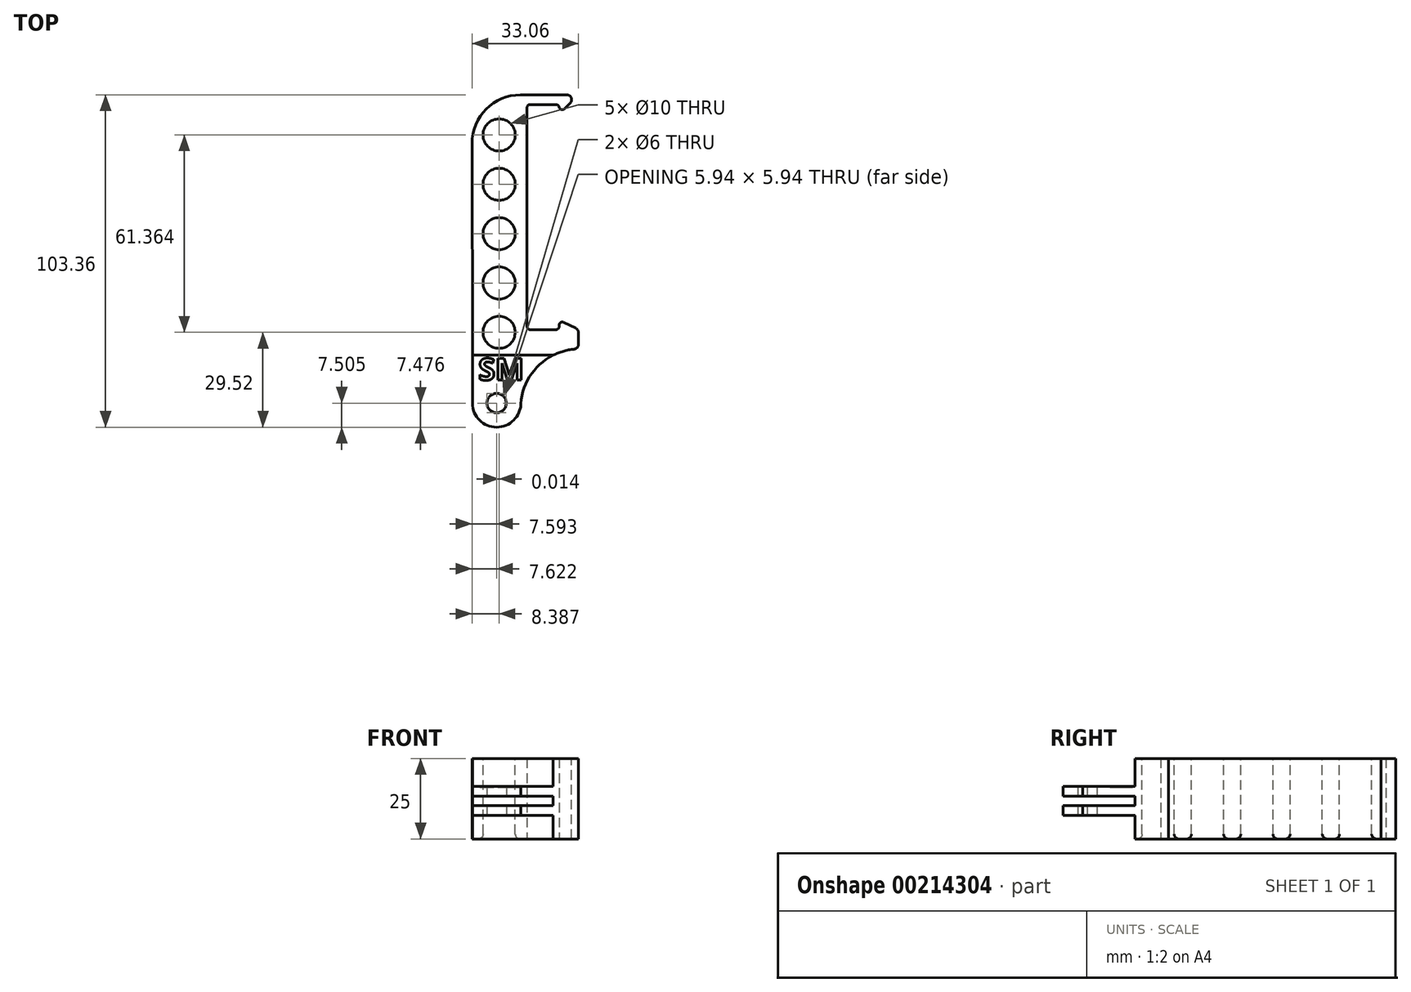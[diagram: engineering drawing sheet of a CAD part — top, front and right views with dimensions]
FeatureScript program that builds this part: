
annotation { "Feature Type Name" : "Feature", "Feature Type Description" : "" }
export const myFeature = defineFeature(function(context is Context, id is Id, definition is map)
    precondition{}
    {
        {
            var Q0;
            Q0=qCreatedBy(makeId("Top.planeOp"),FACE);
            var sketch = newSketch(context, id + "F0", { "sketchPlane" : qUnion([Q0])});
            skLineSegment(sketch, "E0.right", {"start": v(-6.96, 70) * mm, "end": v(-6.96, 0) * mm});
            skLineSegment(sketch, "E1.bottom", {"start": v(-6.96, 0) * mm, "end": v(3.04, 0) * mm});
            skLineSegment(sketch, "E1.right", {"start": v(9.04, 0) * mm, "end": v(9.04, -6) * mm});
            skLineSegment(sketch, "E2.bottom", {"start": v(-6.96, 70) * mm, "end": v(3.04, 70) * mm});
            skLineSegment(sketch, "E2.top", {"start": v(-9, 73) * mm, "end": v(9.04, 73) * mm});
            skLineSegment(sketch, "E3.left", {"start": v(3.04, 70) * mm, "end": v(3.04, 67) * mm});
            skLineSegment(sketch, "E4.left", {"start": v(3.04, 0) * mm, "end": v(3.04, 3) * mm});
            skLineSegment(sketch, "E5.left", {"start": v(-23.9, -7.86) * mm, "end": v(-23.9, -22.86) * mm});
            skLineSegment(sketch, "E5.right", {"start": v(-8.9, -22.86) * mm, "end": v(-8.9, -24.26) * mm});
            skArc(sketch, "E6", {"start": v(-23.9, -22.86) * mm, "mid": v(-16.4, -30.36) * mm, "end": v(-8.9, -22.86) * mm});
            skCircle(sketch, "E7", {"center": v(-16.4, -22.86) * mm, "radius": 3 * mm});
            skPoint(sketch, "E1.top.start.orphan", {"position": v(3.04, -3.63) * mm});
            skLineSegment(sketch, "E8", {"start": v(9.04, 0) * mm, "end": v(3.04, 3) * mm});
            skArc(sketch, "E9", {"start": v(9.04, -6) * mm, "mid": v(-3.66, -11.47) * mm, "end": v(-8.9, -24.26) * mm});
            skPoint(sketch, "E4.right.end.orphan", {"position": v(9.04, -0.42) * mm});
            skLineSegment(sketch, "E10", {"start": v(3.04, 67) * mm, "end": v(9.04, 73) * mm});
            skLineSegment(sketch, "E11.left", {"start": v(-23.9, -7.86) * mm, "end": v(-24.02, 57.9) * mm});
            skArc(sketch, "E12", {"start": v(-9, 73) * mm, "mid": v(-19.63, 68.55) * mm, "end": v(-24.02, 57.9) * mm});
            skSolve(sketch);
        }
        {
            var Q0;
            {var subQ0=sQuery(id+"F0.wireOp",EDGE,"E11.top");Q0=makeQuery(id+"F0.imprint","IMPRINT",FACE,{"disambiguationData":[TD([[makeQuery(id+"F0.imprint","IMPRINT",EDGE,{"derivedFrom":subQ0}),-1.0]])]});}
            var Q1;
            Q1=makeQuery(id+"F0.imprint","IMPRINT",FACE,{"disambiguationData":[TD([[makeQuery(id+"F0.imprint","IMPRINT",EDGE,{"derivedFrom":sQuery(id+"F0.wireOp",EDGE,"E0.right")}),-1.0]])]});
            var Q2;
            {var subQ0=sQuery(id+"F0.wireOp",EDGE,"E11.bottom");Q2=makeQuery(id+"F0.imprint","IMPRINT",FACE,{"disambiguationData":[TD([[makeQuery(id+"F0.imprint","IMPRINT",EDGE,{"derivedFrom":subQ0}),1.0]])]});}
            extrude(context, id + "F1", {"entities" : qUnion([Q0, Q1, Q2]), "depth" : 25 * mm});
        }
        {
            var Q0;
            Q0=makeQuery(id+"F1.opExtrude","SWEPT_FACE",FACE,{"disambiguationData":[OSD([sQuery(id+"F0.wireOp",EDGE,"E5.left")])]});
            var sketch = newSketch(context, id + "F2", { "sketchPlane" : qUnion([Q0])});
            skLineSegment(sketch, "E13.bottom", {"start": v(39.47, 13.32) * mm, "end": v(7.86, 13.32) * mm});
            skLineSegment(sketch, "E13.top", {"start": v(39.47, 10.32) * mm, "end": v(7.86, 10.32) * mm});
            skLineSegment(sketch, "E13.left", {"start": v(7.86, 13.32) * mm, "end": v(7.86, 10.32) * mm});
            skLineSegment(sketch, "E13.right", {"start": v(39.47, 13.32) * mm, "end": v(39.47, 10.32) * mm});
            skLineSegment(sketch, "E14.bottom", {"start": v(7.86, 13.32) * mm, "end": v(39.63, 13.32) * mm});
            skLineSegment(sketch, "E14.top", {"start": v(7.86, 16.32) * mm, "end": v(39.63, 16.32) * mm});
            skLineSegment(sketch, "E14.left", {"start": v(7.86, 13.32) * mm, "end": v(7.86, 16.32) * mm});
            skLineSegment(sketch, "E14.right", {"start": v(39.63, 13.32) * mm, "end": v(39.63, 16.32) * mm});
            skLineSegment(sketch, "E15.bottom", {"start": v(7.86, 10.32) * mm, "end": v(39.63, 10.32) * mm});
            skLineSegment(sketch, "E15.top", {"start": v(7.86, 7.32) * mm, "end": v(39.63, 7.32) * mm});
            skLineSegment(sketch, "E15.left", {"start": v(7.86, 10.32) * mm, "end": v(7.86, 7.32) * mm});
            skLineSegment(sketch, "E15.right", {"start": v(39.63, 10.32) * mm, "end": v(39.63, 7.32) * mm});
            skLineSegment(sketch, "E16.top", {"start": v(7.86, 38.98) * mm, "end": v(39.63, 38.98) * mm});
            skLineSegment(sketch, "E16.left", {"start": v(7.86, 16.32) * mm, "end": v(7.86, 38.98) * mm});
            skLineSegment(sketch, "E16.right", {"start": v(39.63, 16.32) * mm, "end": v(39.63, 38.98) * mm});
            skLineSegment(sketch, "E17.top", {"start": v(7.86, -18.68) * mm, "end": v(39.63, -18.68) * mm});
            skLineSegment(sketch, "E17.left", {"start": v(7.86, 7.32) * mm, "end": v(7.86, -18.68) * mm});
            skLineSegment(sketch, "E17.right", {"start": v(39.63, 7.32) * mm, "end": v(39.63, -18.68) * mm});
            skSolve(sketch);
        }
        {
            var Q0;
            {var subQ1=sQuery(id+"F0.wireOp",EDGE,"E5.left");var subQ6=makeQuery(id+"F1.opExtrude","CAP_EDGE",EDGE,{"disambiguationData":[OSD([subQ1])],"isStart":true});Q0=makeQuery(id+"F2.imprint","IMPRINT",FACE,{"disambiguationData":[TD([[makeQuery(id+"F2.imprint","IMPRINT",EDGE,{"derivedFrom":subQ6}),1.0]])]});}
            var Q1;
            {var subQ1=sQuery(id+"F0.wireOp",EDGE,"E5.left");var subQ6=makeQuery(id+"F1.opExtrude","CAP_EDGE",EDGE,{"disambiguationData":[OSD([subQ1])],"isStart":false});Q1=makeQuery(id+"F2.imprint","IMPRINT",FACE,{"disambiguationData":[TD([[makeQuery(id+"F2.imprint","IMPRINT",EDGE,{"derivedFrom":subQ6}),-1.0]])]});}
            var Q2;
            {var subQ1=sQuery(id+"F2.wireOp",EDGE,"E17.top");Q2=makeQuery(id+"F2.imprint","IMPRINT",FACE,{"disambiguationData":[TD([[makeQuery(id+"F2.imprint","IMPRINT",EDGE,{"derivedFrom":subQ1}),1.0]])]});}
            var Q3;
            {var subQ4=sQuery(id+"F2.wireOp",EDGE,"E16.top");Q3=makeQuery(id+"F2.imprint","IMPRINT",FACE,{"disambiguationData":[TD([[makeQuery(id+"F2.imprint","IMPRINT",EDGE,{"derivedFrom":subQ4}),-1.0]])]});}
            var Q4;
            {var subQ0=sQuery(id+"F2.wireOp",EDGE,"E13.right");Q4=makeQuery(id+"F2.imprint","IMPRINT",FACE,{"disambiguationData":[TD([[makeQuery(id+"F2.imprint","IMPRINT",EDGE,{"derivedFrom":subQ0}),-1.0]])]});}
            var Q5;
            {var subQ0=sQuery(id+"F2.wireOp",EDGE,"E13.left");Q5=makeQuery(id+"F2.imprint","IMPRINT",FACE,{"disambiguationData":[TD([[makeQuery(id+"F2.imprint","IMPRINT",EDGE,{"derivedFrom":subQ0}),1.0]])]});}
            extrude(context, id + "F3", {"entities" : qUnion([Q0, Q1, Q2, Q3, Q4, Q5]), "operationType" : NewBodyOperationType.REMOVE, "oppositeDirection" : true, "depth" : 25 * mm});
        }
        {
            var Q0;
            Q0=makeQuery(id+"F1.opExtrude","SWEPT_EDGE",EDGE,{"disambiguationData":[OSD([sQuery(id+"F0.wireOp",EDGE,"E1.right"),sQuery(id+"F0.wireOp",EDGE,"E8")])]});
            var Q1;
            Q1=makeQuery(id+"F1.opExtrude","SWEPT_EDGE",EDGE,{"disambiguationData":[OSD([sQuery(id+"F0.wireOp",EDGE,"E1.right"),sQuery(id+"F0.wireOp",EDGE,"E9")])]});
            var Q2;
            Q2=makeQuery(id+"F1.opExtrude","SWEPT_EDGE",EDGE,{"disambiguationData":[OSD([sQuery(id+"F0.wireOp",EDGE,"E2.top"),sQuery(id+"F0.wireOp",EDGE,"E10")])]});
            fillet(context, id + "F4", {"entities" : qUnion([Q0, Q1, Q2]), "radius" : 1.5 * mm, "tangentPropagation" : true, "allowEdgeOverflow" : false});
        }
        {
            var Q0;
            Q0=makeQuery(id+"F1.opExtrude","SWEPT_EDGE",EDGE,{"disambiguationData":[OSD([sQuery(id+"F0.wireOp",EDGE,"E0.right"),sQuery(id+"F0.wireOp",EDGE,"E2.bottom")])]});
            var Q1;
            Q1=makeQuery(id+"F1.opExtrude","SWEPT_EDGE",EDGE,{"disambiguationData":[OSD([sQuery(id+"F0.wireOp",EDGE,"E0.right"),sQuery(id+"F0.wireOp",EDGE,"E1.bottom")])]});
            var Q2;
            Q2=makeQuery(id+"F1.opExtrude","SWEPT_EDGE",EDGE,{"disambiguationData":[OSD([sQuery(id+"F0.wireOp",EDGE,"E2.bottom"),sQuery(id+"F0.wireOp",EDGE,"E3.left")])]});
            var Q3;
            Q3=makeQuery(id+"F1.opExtrude","SWEPT_EDGE",EDGE,{"disambiguationData":[OSD([sQuery(id+"F0.wireOp",EDGE,"E1.bottom"),sQuery(id+"F0.wireOp",EDGE,"E4.left")])]});
            fillet(context, id + "F5", {"entities" : qUnion([Q0, Q1, Q2, Q3]), "radius" : 1 * mm, "tangentPropagation" : true, "allowEdgeOverflow" : false});
        }
        {
            var Q0;
            Q0=makeQuery(id+"F1.opExtrude","CAP_FACE",FACE,{"disambiguationData":[OSD([sQuery(id+"F0.wireOp",EDGE,"E0.right"),sQuery(id+"F0.wireOp",EDGE,"E1.bottom"),sQuery(id+"F0.wireOp",EDGE,"E1.right"),sQuery(id+"F0.wireOp",EDGE,"E2.bottom"),sQuery(id+"F0.wireOp",EDGE,"E2.top"),sQuery(id+"F0.wireOp",EDGE,"E2.right"),sQuery(id+"F0.wireOp",EDGE,"E3.top"),sQuery(id+"F0.wireOp",EDGE,"E3.left"),sQuery(id+"F0.wireOp",EDGE,"E4.top"),sQuery(id+"F0.wireOp",EDGE,"E4.left"),sQuery(id+"F0.wireOp",EDGE,"E5.left"),sQuery(id+"F0.wireOp",EDGE,"E5.right"),sQuery(id+"F0.wireOp",EDGE,"E6"),sQuery(id+"F0.wireOp",EDGE,"E7"),sQuery(id+"F0.wireOp",EDGE,"vfLY6uG4-y0tV-8spB-1rVG-UtVCXCo2wCze"),sQuery(id+"F0.wireOp",EDGE,"IZeYfrJS-7V4p-GKvK-Bs6F-KUIEGbjNp2gk"),sQuery(id+"F0.wireOp",EDGE,"UbSuR1B7-Qmw8-mbvo-CxSJ-8DXWhNlOWwhV"),sQuery(id+"F0.wireOp",EDGE,"E8"),sQuery(id+"F0.wireOp",EDGE,"E9"),sQuery(id+"F0.wireOp",EDGE,"E10"),sQuery(id+"F0.wireOp",EDGE,"E11.top"),sQuery(id+"F0.wireOp",EDGE,"E11.left")])],"isStart":false});
            var sketch = newSketch(context, id + "F6", { "sketchPlane" : qUnion([Q0])});
            skLineSegment(sketch, "E18", {"start": v(21.8, 35) * mm, "end": v(-35.74, 35) * mm, "construction": true});
            skLineSegment(sketch, "E19", {"start": v(-15.63, 69.17) * mm, "end": v(-15.43, -43.11) * mm, "construction": true});
            skCircle(sketch, "E20", {"center": v(-15.62, 60.52) * mm, "radius": 5 * mm});
            skCircle(sketch, "E21.0.1.0", {"center": v(-15.62, 45.18) * mm, "radius": 5 * mm});
            skCircle(sketch, "E21.0.2.0", {"center": v(-15.63, 29.84) * mm, "radius": 5 * mm});
            skCircle(sketch, "E21.0.3.0", {"center": v(-15.63, 14.5) * mm, "radius": 5 * mm});
            skCircle(sketch, "E21.0.4.0", {"center": v(-15.63, -0.84) * mm, "radius": 5 * mm});
            skLineSegment(sketch, "E21.direction1", {"start": v(-15.62, 60.52) * mm, "end": v(10.9, 60.52) * mm, "construction": true});
            skLineSegment(sketch, "E21.direction2", {"start": v(-15.62, 60.52) * mm, "end": v(-15.62, 45.18) * mm, "construction": true});
            skSolve(sketch);
        }
        {
            var Q0;
            Q0=makeQuery(id+"F6.imprint","IMPRINT",FACE,{"disambiguationData":[TD([[makeQuery(id+"F6.imprint","IMPRINT",EDGE,{"derivedFrom":sQuery(id+"F6.wireOp",EDGE,"E20")}),1.0]])]});
            var Q1;
            Q1=makeQuery(id+"F6.imprint","IMPRINT",FACE,{"disambiguationData":[TD([[makeQuery(id+"F6.imprint","IMPRINT",EDGE,{"derivedFrom":sQuery(id+"F6.wireOp",EDGE,"E21.0.1.0")}),1.0]])]});
            var Q2;
            Q2=makeQuery(id+"F6.imprint","IMPRINT",FACE,{"disambiguationData":[TD([[makeQuery(id+"F6.imprint","IMPRINT",EDGE,{"derivedFrom":sQuery(id+"F6.wireOp",EDGE,"E21.0.3.0")}),1.0]])]});
            var Q3;
            Q3=makeQuery(id+"F6.imprint","IMPRINT",FACE,{"disambiguationData":[TD([[makeQuery(id+"F6.imprint","IMPRINT",EDGE,{"derivedFrom":sQuery(id+"F6.wireOp",EDGE,"E21.0.4.0")}),1.0]])]});
            var Q4;
            Q4=makeQuery(id+"F6.imprint","IMPRINT",FACE,{"disambiguationData":[TD([[makeQuery(id+"F6.imprint","IMPRINT",EDGE,{"derivedFrom":sQuery(id+"F6.wireOp",EDGE,"E21.0.2.0")}),1.0]])]});
            extrude(context, id + "F7", {"entities" : qUnion([Q0, Q1, Q2, Q3, Q4]), "operationType" : NewBodyOperationType.REMOVE, "oppositeDirection" : true, "depth" : 25 * mm});
        }
        {
            var Q0;
            Q0=makeQuery(id+"F1.opExtrude","SWEPT_EDGE",EDGE,{"disambiguationData":[OSD([sQuery(id+"F0.wireOp",EDGE,"E3.left"),sQuery(id+"F0.wireOp",EDGE,"E10")])]});
            var Q1;
            Q1=makeQuery(id+"F1.opExtrude","SWEPT_EDGE",EDGE,{"disambiguationData":[OSD([sQuery(id+"F0.wireOp",EDGE,"E4.left"),sQuery(id+"F0.wireOp",EDGE,"E8")])]});
            fillet(context, id + "F8", {"entities" : qUnion([Q0, Q1]), "radius" : 1 * mm, "tangentPropagation" : true, "allowEdgeOverflow" : false});
        }
        {
            var Q0;
            Q0=makeQuery(id+"F7.boolean.opBoolean","COPY",EDGE,{"derivedFrom":makeQuery(id+"F7.opExtrude","CAP_EDGE",EDGE,{"disambiguationData":[OSD([sQuery(id+"F6.wireOp",EDGE,"E20")])],"isStart":true})});
            var Q1;
            Q1=makeQuery(id+"F7.boolean.opBoolean","COPY",EDGE,{"derivedFrom":makeQuery(id+"F7.opExtrude","CAP_EDGE",EDGE,{"disambiguationData":[OSD([sQuery(id+"F6.wireOp",EDGE,"E21.0.1.0")])],"isStart":true})});
            var Q2;
            Q2=makeQuery(id+"F7.boolean.opBoolean","COPY",EDGE,{"derivedFrom":makeQuery(id+"F7.opExtrude","CAP_EDGE",EDGE,{"disambiguationData":[OSD([sQuery(id+"F6.wireOp",EDGE,"E21.0.2.0")])],"isStart":true})});
            var Q3;
            Q3=makeQuery(id+"F7.boolean.opBoolean","COPY",EDGE,{"derivedFrom":makeQuery(id+"F7.opExtrude","CAP_EDGE",EDGE,{"disambiguationData":[OSD([sQuery(id+"F6.wireOp",EDGE,"E21.0.3.0")])],"isStart":true})});
            var Q4;
            Q4=makeQuery(id+"F7.boolean.opBoolean","COPY",EDGE,{"derivedFrom":makeQuery(id+"F7.opExtrude","CAP_EDGE",EDGE,{"disambiguationData":[OSD([sQuery(id+"F6.wireOp",EDGE,"E21.0.4.0")])],"isStart":true})});
            var Q5;
            Q5=makeQuery(id+"F7.boolean.opBoolean","INTERSECT",EDGE,{"derivedFrom":[makeQuery(id+"F1.opExtrude","CAP_FACE",FACE,{"disambiguationData":[OSD([sQuery(id+"F0.wireOp",EDGE,"E0.right"),sQuery(id+"F0.wireOp",EDGE,"E1.bottom"),sQuery(id+"F0.wireOp",EDGE,"E1.right"),sQuery(id+"F0.wireOp",EDGE,"E2.bottom"),sQuery(id+"F0.wireOp",EDGE,"E2.top"),sQuery(id+"F0.wireOp",EDGE,"E3.left"),sQuery(id+"F0.wireOp",EDGE,"E4.left"),sQuery(id+"F0.wireOp",EDGE,"E5.left"),sQuery(id+"F0.wireOp",EDGE,"E6"),sQuery(id+"F0.wireOp",EDGE,"E7"),sQuery(id+"F0.wireOp",EDGE,"E8"),sQuery(id+"F0.wireOp",EDGE,"E9"),sQuery(id+"F0.wireOp",EDGE,"E10"),sQuery(id+"F0.wireOp",EDGE,"E11.left"),sQuery(id+"F0.wireOp",EDGE,"E12")])],"isStart":true}),makeQuery(id+"F7.opExtrude","SWEPT_FACE",FACE,{"disambiguationData":[OSD([sQuery(id+"F6.wireOp",EDGE,"E20")])]})]});
            var Q6;
            Q6=makeQuery(id+"F7.boolean.opBoolean","INTERSECT",EDGE,{"derivedFrom":[makeQuery(id+"F1.opExtrude","CAP_FACE",FACE,{"disambiguationData":[OSD([sQuery(id+"F0.wireOp",EDGE,"E0.right"),sQuery(id+"F0.wireOp",EDGE,"E1.bottom"),sQuery(id+"F0.wireOp",EDGE,"E1.right"),sQuery(id+"F0.wireOp",EDGE,"E2.bottom"),sQuery(id+"F0.wireOp",EDGE,"E2.top"),sQuery(id+"F0.wireOp",EDGE,"E3.left"),sQuery(id+"F0.wireOp",EDGE,"E4.left"),sQuery(id+"F0.wireOp",EDGE,"E5.left"),sQuery(id+"F0.wireOp",EDGE,"E6"),sQuery(id+"F0.wireOp",EDGE,"E7"),sQuery(id+"F0.wireOp",EDGE,"E8"),sQuery(id+"F0.wireOp",EDGE,"E9"),sQuery(id+"F0.wireOp",EDGE,"E10"),sQuery(id+"F0.wireOp",EDGE,"E11.left"),sQuery(id+"F0.wireOp",EDGE,"E12")])],"isStart":true}),makeQuery(id+"F7.opExtrude","SWEPT_FACE",FACE,{"disambiguationData":[OSD([sQuery(id+"F6.wireOp",EDGE,"E21.0.1.0")])]})]});
            var Q7;
            Q7=makeQuery(id+"F7.boolean.opBoolean","INTERSECT",EDGE,{"derivedFrom":[makeQuery(id+"F1.opExtrude","CAP_FACE",FACE,{"disambiguationData":[OSD([sQuery(id+"F0.wireOp",EDGE,"E0.right"),sQuery(id+"F0.wireOp",EDGE,"E1.bottom"),sQuery(id+"F0.wireOp",EDGE,"E1.right"),sQuery(id+"F0.wireOp",EDGE,"E2.bottom"),sQuery(id+"F0.wireOp",EDGE,"E2.top"),sQuery(id+"F0.wireOp",EDGE,"E3.left"),sQuery(id+"F0.wireOp",EDGE,"E4.left"),sQuery(id+"F0.wireOp",EDGE,"E5.left"),sQuery(id+"F0.wireOp",EDGE,"E6"),sQuery(id+"F0.wireOp",EDGE,"E7"),sQuery(id+"F0.wireOp",EDGE,"E8"),sQuery(id+"F0.wireOp",EDGE,"E9"),sQuery(id+"F0.wireOp",EDGE,"E10"),sQuery(id+"F0.wireOp",EDGE,"E11.left"),sQuery(id+"F0.wireOp",EDGE,"E12")])],"isStart":true}),makeQuery(id+"F7.opExtrude","SWEPT_FACE",FACE,{"disambiguationData":[OSD([sQuery(id+"F6.wireOp",EDGE,"E21.0.2.0")])]})]});
            var Q8;
            Q8=makeQuery(id+"F7.boolean.opBoolean","INTERSECT",EDGE,{"derivedFrom":[makeQuery(id+"F1.opExtrude","CAP_FACE",FACE,{"disambiguationData":[OSD([sQuery(id+"F0.wireOp",EDGE,"E0.right"),sQuery(id+"F0.wireOp",EDGE,"E1.bottom"),sQuery(id+"F0.wireOp",EDGE,"E1.right"),sQuery(id+"F0.wireOp",EDGE,"E2.bottom"),sQuery(id+"F0.wireOp",EDGE,"E2.top"),sQuery(id+"F0.wireOp",EDGE,"E3.left"),sQuery(id+"F0.wireOp",EDGE,"E4.left"),sQuery(id+"F0.wireOp",EDGE,"E5.left"),sQuery(id+"F0.wireOp",EDGE,"E6"),sQuery(id+"F0.wireOp",EDGE,"E7"),sQuery(id+"F0.wireOp",EDGE,"E8"),sQuery(id+"F0.wireOp",EDGE,"E9"),sQuery(id+"F0.wireOp",EDGE,"E10"),sQuery(id+"F0.wireOp",EDGE,"E11.left"),sQuery(id+"F0.wireOp",EDGE,"E12")])],"isStart":true}),makeQuery(id+"F7.opExtrude","SWEPT_FACE",FACE,{"disambiguationData":[OSD([sQuery(id+"F6.wireOp",EDGE,"E21.0.3.0")])]})]});
            var Q9;
            Q9=makeQuery(id+"F7.boolean.opBoolean","INTERSECT",EDGE,{"derivedFrom":[makeQuery(id+"F1.opExtrude","CAP_FACE",FACE,{"disambiguationData":[OSD([sQuery(id+"F0.wireOp",EDGE,"E0.right"),sQuery(id+"F0.wireOp",EDGE,"E1.bottom"),sQuery(id+"F0.wireOp",EDGE,"E1.right"),sQuery(id+"F0.wireOp",EDGE,"E2.bottom"),sQuery(id+"F0.wireOp",EDGE,"E2.top"),sQuery(id+"F0.wireOp",EDGE,"E3.left"),sQuery(id+"F0.wireOp",EDGE,"E4.left"),sQuery(id+"F0.wireOp",EDGE,"E5.left"),sQuery(id+"F0.wireOp",EDGE,"E6"),sQuery(id+"F0.wireOp",EDGE,"E7"),sQuery(id+"F0.wireOp",EDGE,"E8"),sQuery(id+"F0.wireOp",EDGE,"E9"),sQuery(id+"F0.wireOp",EDGE,"E10"),sQuery(id+"F0.wireOp",EDGE,"E11.left"),sQuery(id+"F0.wireOp",EDGE,"E12")])],"isStart":true}),makeQuery(id+"F7.opExtrude","SWEPT_FACE",FACE,{"disambiguationData":[OSD([sQuery(id+"F6.wireOp",EDGE,"E21.0.4.0")])]})]});
            fillet(context, id + "F9", {"entities" : qUnion([Q0, Q1, Q2, Q3, Q4, Q5, Q6, Q7, Q8, Q9]), "radius" : 1.5 * mm, "tangentPropagation" : true, "allowEdgeOverflow" : false});
        }
        {
            var Q0;
            Q0=makeQuery(id+"F3.boolean.opBoolean","COPY",FACE,{"derivedFrom":makeQuery(id+"F3.opExtrude","SWEPT_FACE",FACE,{"disambiguationData":[OSD([sQuery(id+"F2.wireOp",EDGE,"E14.top")])]})});
            var sketch = newSketch(context, id + "F10", { "sketchPlane" : qUnion([Q0])});
            skText(sketch, "E22", { "text": "SM", "fontName": "OpenSans-Bold.ttf"});
            const initialGuessF10  = {"E22": [-0.02207, -0.01571, 1, 0, 0.00683]};
            skSetInitialGuess(sketch, initialGuessF10);
            skSolve(sketch);
        }
        {
            var Q0;
            Q0=makeQuery(id+"F10.imprint","IMPRINT",FACE,{"disambiguationData":[TD([[makeQuery(id+"F10.imprint","IMPRINT",EDGE,{"derivedFrom":sQuery(id+"F10.wireOp",EDGE,"E22.sketch_text.stroke-0")}),-1.0]])]});
            var Q1;
            Q1=makeQuery(id+"F10.imprint","IMPRINT",FACE,{"disambiguationData":[TD([[makeQuery(id+"F10.imprint","IMPRINT",EDGE,{"derivedFrom":sQuery(id+"F10.wireOp",EDGE,"E22.sketch_text.stroke-28")}),-1.0]])]});
            extrude(context, id + "F11", {"entities" : qUnion([Q0, Q1]), "operationType" : NewBodyOperationType.REMOVE, "oppositeDirection" : true, "depth" : 0.25 * mm});
        }
    });
